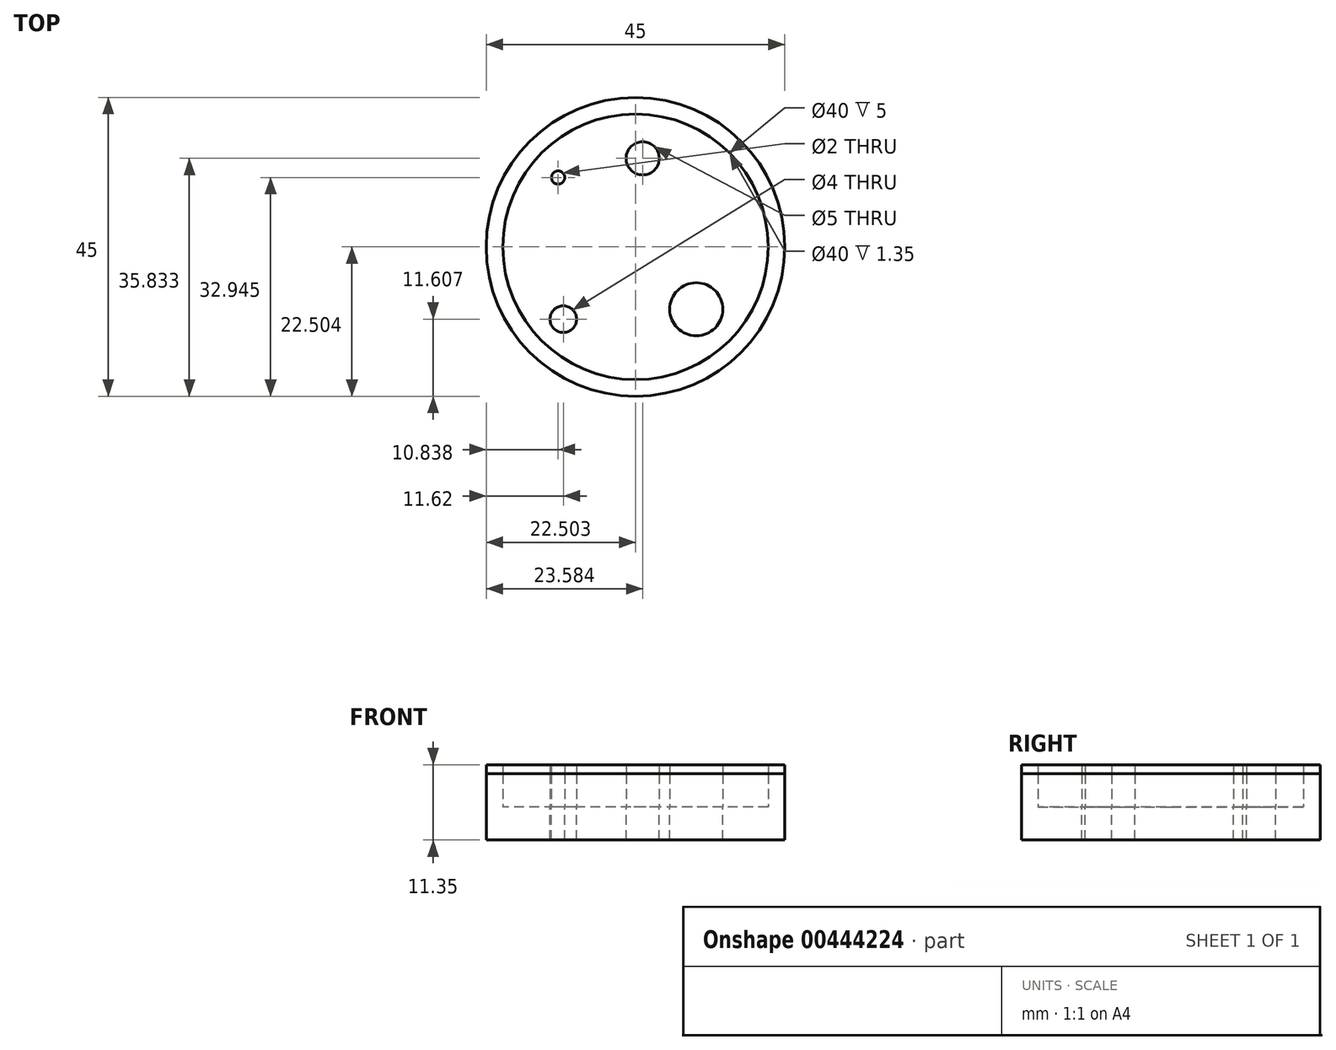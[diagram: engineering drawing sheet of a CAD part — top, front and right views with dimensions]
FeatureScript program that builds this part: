
annotation { "Feature Type Name" : "Feature", "Feature Type Description" : "" }
export const myFeature = defineFeature(function(context is Context, id is Id, definition is map)
    precondition{}
    {
        {
            var Q0;
            Q0=qCreatedBy(makeId("Top.planeOp"),FACE);
            var sketch = newSketch(context, id + "F0", { "sketchPlane" : qUnion([Q0])});
            skCircle(sketch, "E0", {"center": v(-20.9, 13.65) * mm, "radius": 22.5 * mm});
            skCircle(sketch, "E1", {"center": v(-20.9, 13.65) * mm, "radius": 20 * mm});
            skCircle(sketch, "E2", {"center": v(-32.57, 24.1) * mm, "radius": 1 * mm});
            skCircle(sketch, "E3", {"center": v(-11.75, 4.25) * mm, "radius": 4 * mm});
            skCircle(sketch, "E4", {"center": v(-31.79, 2.76) * mm, "radius": 2 * mm});
            skCircle(sketch, "E5", {"center": v(-19.83, 26.98) * mm, "radius": 2.5 * mm});
            skSolve(sketch);
        }
        {
            var Q0;
            Q0=makeQuery(id+"F0.imprint","IMPRINT",FACE,{"disambiguationData":[TD([[makeQuery(id+"F0.imprint","IMPRINT",EDGE,{"derivedFrom":sQuery(id+"F0.wireOp",EDGE,"E0")}),1.0]])]});
            var Q1;
            Q1=makeQuery(id+"F0.imprint","IMPRINT",FACE,{"disambiguationData":[TD([[makeQuery(id+"F0.imprint","IMPRINT",EDGE,{"derivedFrom":sQuery(id+"F0.wireOp",EDGE,"E3")}),1.0]])]});
            var Q2;
            Q2=makeQuery(id+"F0.imprint","IMPRINT",FACE,{"disambiguationData":[TD([[makeQuery(id+"F0.imprint","IMPRINT",EDGE,{"derivedFrom":sQuery(id+"F0.wireOp",EDGE,"E5")}),1.0]])]});
            var Q3;
            Q3=makeQuery(id+"F0.imprint","IMPRINT",FACE,{"disambiguationData":[TD([[makeQuery(id+"F0.imprint","IMPRINT",EDGE,{"derivedFrom":sQuery(id+"F0.wireOp",EDGE,"E2")}),1.0]])]});
            var Q4;
            Q4=makeQuery(id+"F0.imprint","IMPRINT",FACE,{"disambiguationData":[TD([[makeQuery(id+"F0.imprint","IMPRINT",EDGE,{"derivedFrom":sQuery(id+"F0.wireOp",EDGE,"E4")}),1.0]])]});
            extrude(context, id + "F1", {"entities" : qUnion([Q0, Q1, Q2, Q3, Q4]), "depth" : 5 * mm});
        }
        {
            var Q0;
            Q0=makeQuery(id+"F1.opExtrude","CAP_FACE",FACE,{"disambiguationData":[OSD([sQuery(id+"F0.wireOp",EDGE,"E0"),sQuery(id+"F0.wireOp",EDGE,"E1")])],"isStart":false});
            var Q1;
            Q1=makeQuery(id+"F0.imprint","IMPRINT",FACE,{"disambiguationData":[TD([[makeQuery(id+"F0.imprint","IMPRINT",EDGE,{"derivedFrom":sQuery(id+"F0.wireOp",EDGE,"E1")}),1.0]])]});
            var Q2;
            Q2=makeQuery(id+"F0.imprint","IMPRINT",FACE,{"disambiguationData":[TD([[makeQuery(id+"F0.imprint","IMPRINT",EDGE,{"derivedFrom":sQuery(id+"F0.wireOp",EDGE,"E0")}),1.0]])]});
            extrude(context, id + "F2", {"entities" : qUnion([Q0, Q1, Q2]), "operationType" : NewBodyOperationType.ADD, "oppositeDirection" : true, "depth" : 5 * mm});
        }
        {
            var Q0;
            Q0=makeQuery(id+"F0.imprint","IMPRINT",FACE,{"disambiguationData":[TD([[makeQuery(id+"F0.imprint","IMPRINT",EDGE,{"derivedFrom":sQuery(id+"F0.wireOp",EDGE,"E3")}),1.0]])]});
            extrude(context, id + "F3", {"entities" : qUnion([Q0]), "operationType" : NewBodyOperationType.ADD, "oppositeDirection" : true, "depth" : 5 * mm});
        }
        {
            var Q0;
            Q0=sQuery(id+"F0.wireOp",EDGE,"E3");
            var Q1;
            Q1=sQuery(id+"F0.wireOp",EDGE,"E4");
            var Q2;
            Q2=sQuery(id+"F0.wireOp",EDGE,"E2");
            var Q3;
            Q3=sQuery(id+"F0.wireOp",EDGE,"E5");
            extrude(context, id + "F4", {"bodyType" : ToolBodyType.SURFACE, "surfaceEntities" : qUnion([Q0, Q1, Q2, Q3]), "oppositeDirection" : true, "depth" : 5 * mm});
        }
        {
            var Q0;
            Q0=makeQuery(id+"F0.imprint","IMPRINT",FACE,{"disambiguationData":[TD([[makeQuery(id+"F0.imprint","IMPRINT",EDGE,{"derivedFrom":sQuery(id+"F0.wireOp",EDGE,"E3")}),1.0]])]});
            var Q1;
            Q1=makeQuery(id+"F0.imprint","IMPRINT",FACE,{"disambiguationData":[TD([[makeQuery(id+"F0.imprint","IMPRINT",EDGE,{"derivedFrom":sQuery(id+"F0.wireOp",EDGE,"E4")}),1.0]])]});
            var Q2;
            Q2=makeQuery(id+"F0.imprint","IMPRINT",FACE,{"disambiguationData":[TD([[makeQuery(id+"F0.imprint","IMPRINT",EDGE,{"derivedFrom":sQuery(id+"F0.wireOp",EDGE,"E2")}),1.0]])]});
            var Q3;
            Q3=makeQuery(id+"F0.imprint","IMPRINT",FACE,{"disambiguationData":[TD([[makeQuery(id+"F0.imprint","IMPRINT",EDGE,{"derivedFrom":sQuery(id+"F0.wireOp",EDGE,"E5")}),1.0]])]});
            extrude(context, id + "F5", {"entities" : qUnion([Q0, Q1, Q2, Q3]), "oppositeDirection" : true, "depth" : 5 * mm});
        }
        {
            var Q0;
            Q0=makeQuery(id+"F1.opExtrude","CAP_FACE",FACE,{"disambiguationData":[OSD([sQuery(id+"F0.wireOp",EDGE,"E0"),sQuery(id+"F0.wireOp",EDGE,"E1")])],"isStart":false});
            var Q1;
            Q1=makeQuery(id+"F1.opExtrude","CAP_FACE",FACE,{"disambiguationData":[OSD([sQuery(id+"F0.wireOp",EDGE,"E4")])],"isStart":false});
            var Q2;
            Q2=makeQuery(id+"F1.opExtrude","CAP_FACE",FACE,{"disambiguationData":[OSD([sQuery(id+"F0.wireOp",EDGE,"E2")])],"isStart":false});
            var Q3;
            Q3=makeQuery(id+"F1.opExtrude","CAP_FACE",FACE,{"disambiguationData":[OSD([sQuery(id+"F0.wireOp",EDGE,"E3")])],"isStart":false});
            var Q4;
            Q4=makeQuery(id+"F1.opExtrude","CAP_FACE",FACE,{"disambiguationData":[OSD([sQuery(id+"F0.wireOp",EDGE,"E5")])],"isStart":false});
            extrude(context, id + "F6", {"entities" : qUnion([Q0, Q1, Q2, Q3, Q4]), "depth" : 1.35 * mm});
        }
    });
